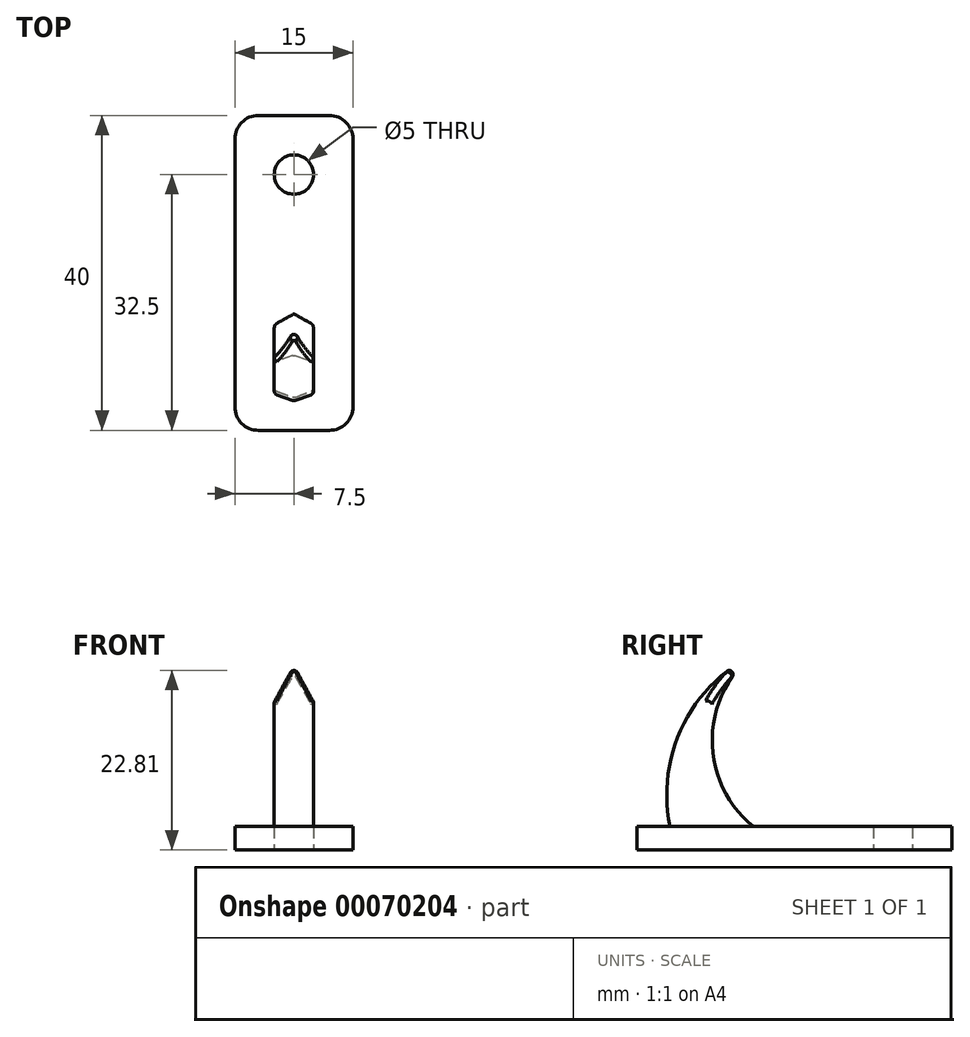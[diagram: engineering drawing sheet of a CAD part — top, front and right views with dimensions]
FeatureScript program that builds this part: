
annotation { "Feature Type Name" : "Feature", "Feature Type Description" : "" }
export const myFeature = defineFeature(function(context is Context, id is Id, definition is map)
    precondition{}
    {
        {
            var Q0;
            Q0=qCreatedBy(makeId("Right.planeOp"),FACE);
            var sketch = newSketch(context, id + "F0", { "sketchPlane" : qUnion([Q0])});
            skArc(sketch, "E0", {"start": v(0, 25) * mm, "mid": v(-4.43, 8.73) * mm, "end": v(10, 0) * mm});
            skArc(sketch, "E1", {"start": v(0, 25) * mm, "mid": v(-9.84, 14.43) * mm, "end": v(-10, 0) * mm});
            skLineSegment(sketch, "E2", {"start": v(-10, 0) * mm, "end": v(10, 0) * mm});
            skSolve(sketch);
        }
        {
            var Q0;
            Q0=makeQuery(id+"F0.imprint","IMPRINT",FACE,{"disambiguationData":[TD([[makeQuery(id+"F0.imprint","IMPRINT",EDGE,{"derivedFrom":sQuery(id+"F0.wireOp",EDGE,"E0")}),-1.0]])]});
            extrude(context, id + "F1", {"entities" : qUnion([Q0]), "offsetDistance" : 25 * mm, "depth" : 5 * mm, "hasDraft" : true, "draftAngle" : 20 * degree, "draftPullDirection" : true, "symmetric" : true});
        }
        {
            var Q0;
            Q0=qCreatedBy(makeId("Top.planeOp"),FACE);
            var sketch = newSketch(context, id + "F2", { "sketchPlane" : qUnion([Q0])});
            skLineSegment(sketch, "E3.rect.bottom", {"start": v(4.5, -15) * mm, "end": v(-4.5, -15) * mm});
            skLineSegment(sketch, "E3.rect.top", {"start": v(4.5, 25) * mm, "end": v(-4.5, 25) * mm});
            skLineSegment(sketch, "E3.rect.left", {"start": v(7.5, -12) * mm, "end": v(7.5, 22) * mm});
            skLineSegment(sketch, "E3.rect.right", {"start": v(-7.5, -12) * mm, "end": v(-7.5, 22) * mm});
            skPoint(sketch, "E3.rect.middle", {"position": v(0, 5) * mm});
            skPoint(sketch, "E4.visualSharp", {"position": v(-7.5, -15) * mm});
            skArc(sketch, "E4.filletArc", {"start": v(-7.5, -12) * mm, "mid": v(-6.62, -14.12) * mm, "end": v(-4.5, -15) * mm});
            skPoint(sketch, "E5.visualSharp", {"position": v(7.5, -15) * mm});
            skArc(sketch, "E5.filletArc", {"start": v(4.5, -15) * mm, "mid": v(6.62, -14.12) * mm, "end": v(7.5, -12) * mm});
            skPoint(sketch, "E6.visualSharp", {"position": v(-7.5, 25) * mm});
            skArc(sketch, "E6.filletArc", {"start": v(-4.5, 25) * mm, "mid": v(-6.62, 24.12) * mm, "end": v(-7.5, 22) * mm});
            skPoint(sketch, "E7.visualSharp", {"position": v(7.5, 25) * mm});
            skArc(sketch, "E7.filletArc", {"start": v(7.5, 22) * mm, "mid": v(6.62, 24.12) * mm, "end": v(4.5, 25) * mm});
            skCircle(sketch, "E8", {"center": v(0, 17.5) * mm, "radius": 2.5 * mm});
            skSolve(sketch);
        }
        {
            var Q0;
            Q0=makeQuery(id+"F2.imprint","IMPRINT",FACE,{"disambiguationData":[TD([[makeQuery(id+"F2.imprint","IMPRINT",EDGE,{"derivedFrom":sQuery(id+"F2.wireOp",EDGE,"E3.rect.bottom")}),-1.0]])]});
            extrude(context, id + "F3", {"entities" : qUnion([Q0]), "operationType" : NewBodyOperationType.ADD, "depth" : 3 * mm});
        }
        {
            var Q0;
            {var subQ0=makeQuery(id+"F1.opExtrude","SWEPT_FACE",FACE,{"disambiguationData":[OSD([sQuery(id+"F0.wireOp",EDGE,"E0")])]});Q0=makeQuery(id+"F1.*.booleanUnion.opBoolean","MERGE",EDGE,{"derivedFrom":[makeQuery(id+"F1.*.split.splitOp","SPLIT_SURFACE_INTERSECT",EDGE,{"derivedFrom":[subQ0]}),makeQuery(id+"F1.*.split.splitOp","SPLIT_SURFACE_INTERSECT",EDGE,{"derivedFrom":[subQ0],"isFromBackBody":true})]});}
            var Q1;
            {var subQ0=makeQuery(id+"F1.opExtrude","SWEPT_FACE",FACE,{"disambiguationData":[OSD([sQuery(id+"F0.wireOp",EDGE,"E1")])]});Q1=makeQuery(id+"F1.*.booleanUnion.opBoolean","MERGE",EDGE,{"derivedFrom":[makeQuery(id+"F1.*.split.splitOp","SPLIT_SURFACE_INTERSECT",EDGE,{"derivedFrom":[subQ0]}),makeQuery(id+"F1.*.split.splitOp","SPLIT_SURFACE_INTERSECT",EDGE,{"derivedFrom":[subQ0],"isFromBackBody":true})]});}
            var Q2;
            Q2=makeQuery(id+"F1.opExtrude","CAP_EDGE",EDGE,{"disambiguationData":[OSD([sQuery(id+"F0.wireOp",EDGE,"E0")])],"isStart":true});
            var Q3;
            Q3=makeQuery(id+"F1.opExtrude","CAP_EDGE",EDGE,{"disambiguationData":[OSD([sQuery(id+"F0.wireOp",EDGE,"E0")])],"isStart":false});
            var Q4;
            Q4=makeQuery(id+"F1.opExtrude","CAP_EDGE",EDGE,{"disambiguationData":[OSD([sQuery(id+"F0.wireOp",EDGE,"E1")])],"isStart":false});
            var Q5;
            Q5=makeQuery(id+"F1.opExtrude","CAP_EDGE",EDGE,{"disambiguationData":[OSD([sQuery(id+"F0.wireOp",EDGE,"E1")])],"isStart":true});
            var Q6;
            Q6=makeQuery(id+"F1.*.split.splitOp","SPLIT",EDGE,{"derivedFrom":makeQuery(id+"F1.opExtrude","SWEPT_EDGE",EDGE,{"disambiguationData":[OSD([sQuery(id+"F0.wireOp",EDGE,"E0"),sQuery(id+"F0.wireOp",EDGE,"E1")])]}),"isFromBackBody":true});
            var Q7;
            Q7=makeQuery(id+"F1.*.split.splitOp","SPLIT",EDGE,{"derivedFrom":makeQuery(id+"F1.opExtrude","SWEPT_EDGE",EDGE,{"disambiguationData":[OSD([sQuery(id+"F0.wireOp",EDGE,"E0"),sQuery(id+"F0.wireOp",EDGE,"E1")])]})});
            fillet(context, id + "F4", {"entities" : qUnion([Q0, Q1, Q2, Q3, Q4, Q5, Q6, Q7]), "radius" : .5 * mm, "tangentPropagation" : true, "allowEdgeOverflow" : false});
        }
    });
